# Revit family: PRD_FrankeWS_TltRllHldrs_CUBUSToiletRollHolder_CUBX111HP
name_source: partatom
category: Specialty Equipment
revit_build: Autodesk Revit 2018 (Build: 20190510_1515(x64)
units: mm (PartAtom-declared; Revit-internal decimal feet)

## family parameters
Cut with Voids When Loaded = No
Host = Face
OmniClass Number = 23.40.20.21.21
OmniClass Title = Toilet Paper Dispensers
Part Type = Normal
Room Calculation Point = No
Round Connector Dimension = Use Diameter
Shared = No

## types (1)
- CUBX111HP
    AssetType = Fixed
    BIMObjectName = PRD_AR_ToiletRollHolders_CUBUSToiletRollHolder_CUBX111HP
    Category = Pr_40_20_76_88, Toilet roll holders
    Default Elevation = 600 mm
    Description = Toilet roll holder for wall mounting, 304 stainless steel, for 1 roll with max. diameter 130 mm, stainless steel folding cover, square cover with drilled hole on bottom for fixation, inclusive stainless steel screws and dowels.
    DurationUnit = year
    Features = stainless steel, surface high polished
    FillingQuantity = 1
    Finish = high polished
    GrossWeight = 0.52 kg
    HolderMaterial = PRD_AR_StainlessSteel_HighPolished
    IfcExportAs = IfcFurnitureType
    IfcExportType = USERDEFINED
    IntegralAccessories = incl. stainless steel screws and dowels
    IsBuiltIn = TRUE
    Lock = No lock
    MainColor = stainless steel
    Manufacturer = KWC Group AG
    ManufacturerName = KWC Group AG
    ManufacturerURL = www.kwc.com
    Material = stainless steel
    MaterialCode = 1.4301
    Model = CUBX111HP
    ModelNumber = 2000106363
    ModelReference = CUBX111HP
    NBSDescription = Toilet roll holders
    NBSReference = 45-35-72/368
    Name = Toilet roll holder CUBX111HP
    NetWeight = 0.39 kg
    NominalDepth = 179 mm  [stored 0.58727 ft]
    NominalHeight = 54 mm  [stored 0.177165 ft]
    NominalWidth = 165 mm
    ProductInformation = https://pim.kwc.com
    Size = 165 x 54 x 179 mm
    Spindle = No
    Style = Roll holder
    ToiletRollMaterial = PRD_FrankeWS_ToiletRoll
    TypeOfFixing = Screw
    TypeOfMounting = Wall mounting
    URL = www.kwc.com
    Uniclass2015Code = Pr_40_20_76_88
    Uniclass2015Title = Toilet roll holders
    Uniclass2015Version = Products v1.17
    Version = 1
    WarrantyDurationUnit = year

note: [stored X ft] marks values corroborated as IEEE doubles in the binary element streams (Revit-internal decimal feet)

## geometry (parser evidence)
native form markers: Sweep x1
no freeform markers — native parametric forms only
